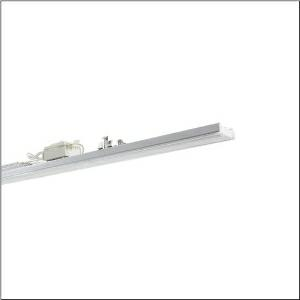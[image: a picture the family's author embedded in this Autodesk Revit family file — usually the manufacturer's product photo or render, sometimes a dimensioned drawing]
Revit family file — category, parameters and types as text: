
# Revit family: licross_r__21_recessed_ho_52te1edv4l2s_2def
name_source: partatom
category: Lighting Fixtures
units: mm (PartAtom-declared; Revit-internal decimal feet)

## family parameters
Cut with Voids When Loaded = No
Host = Face
Light Source = No
Part Type = Normal
Room Calculation Point = No
Round Connector Dimension = Use Diameter
Shared = No

## types (1)
- --- (1 x LED, 22130 lm, 125.6 W, 4000K)
    Apparent Load = 126 VA
    CIE Flux Codes = 85 95 99 100 100
    Color Rendering = 80
    Color Temperature = 4000K
    Default Elevation = 1800 mm
    Description = Licross® 21 Recessed HO, luminaire insert, of sheet steel, galvanised, coil coated, white, length: 2.250mm, width: 66mm, height: 67mm, LED rated luminous flux: 22.130lm, light colour: 840, control gear: DALI 2, with plug, 5-pole, with phase selection, mains connection: 220..240V, AC, 50/60Hz, rated input power: 126W, internal wiring halogen-free, primary light control with lens, of plastic, primary optical cover: cover, of PMMA, light emission: direct distribution, primary light characteristic: symmetric, protection rating (complete): IP54, insulation class (complete): insulation class I (protective earthing), certification: CE, ENEC, VDE, UKCA, protection symbol: D if used in an environment with non-conductive dust loads with corresponding accessories, impact resistance: IK06, permissible ambient temperature for indoor applications: -40..+30°C, corresponds to IFS (International Featured Standards) requirements for safety and quality in the food industry, reducing of maximum allowable ambient temperature of 5°C with ceiling mounting, LABS conformity tested according to VDMA 24364:2018-05, packaging unit: 1 piece
    Height = 58 mm
    Lamp = 1 x LED
    Lamp Light Flux = 22130 lm
    Lamp Power = 125.6 W
    Lamp count = 1
    Length = 2250 mm
    Luminous efficacy = 176 lm/W
    Manufacturer = Siteco
    ModVariant = No
    Model = 52TE1EDV4L2S
    Mounting Place = Ceiling
    Mounting Type = Pendant
    Number of Poles = 1
    OnlyDefault = Yes
    Power Factor = 1
    Product Name = Licross® 21 Recessed HO
    Product group = luminaire insert | ceiling pendant
    ProductGroupID = 902
    Protection Class = Protection class I
    Protection Degree = IP 54
    RLX_Detail_Level = 1
    RLX_Emergency_Light_Flux = 0 lm
    RLX_Emergency_Type = 0
    RLX_Emergency_Type_DB = No
    RlxData = <blob elided: 29529 chars, md5=9c5e4190>
    Socket = socket
    Standby Power = 0 W
    System Light Flux = 22129 lm
    System Power = 126 W
    Type Comments = factory setting: luminous flux: 100 % | dim-lin: 254 | 489 mA
    Type Image = l_1296930.jpg
    URL = http://relux.com
    VarID = @adj_146943
    Voltage = 0 V
    Weight = 0.00 kg
    Width = 66 mm

## geometry (parser evidence)
native form markers: Blend x4, Sweep x11
no freeform markers — native parametric forms only
